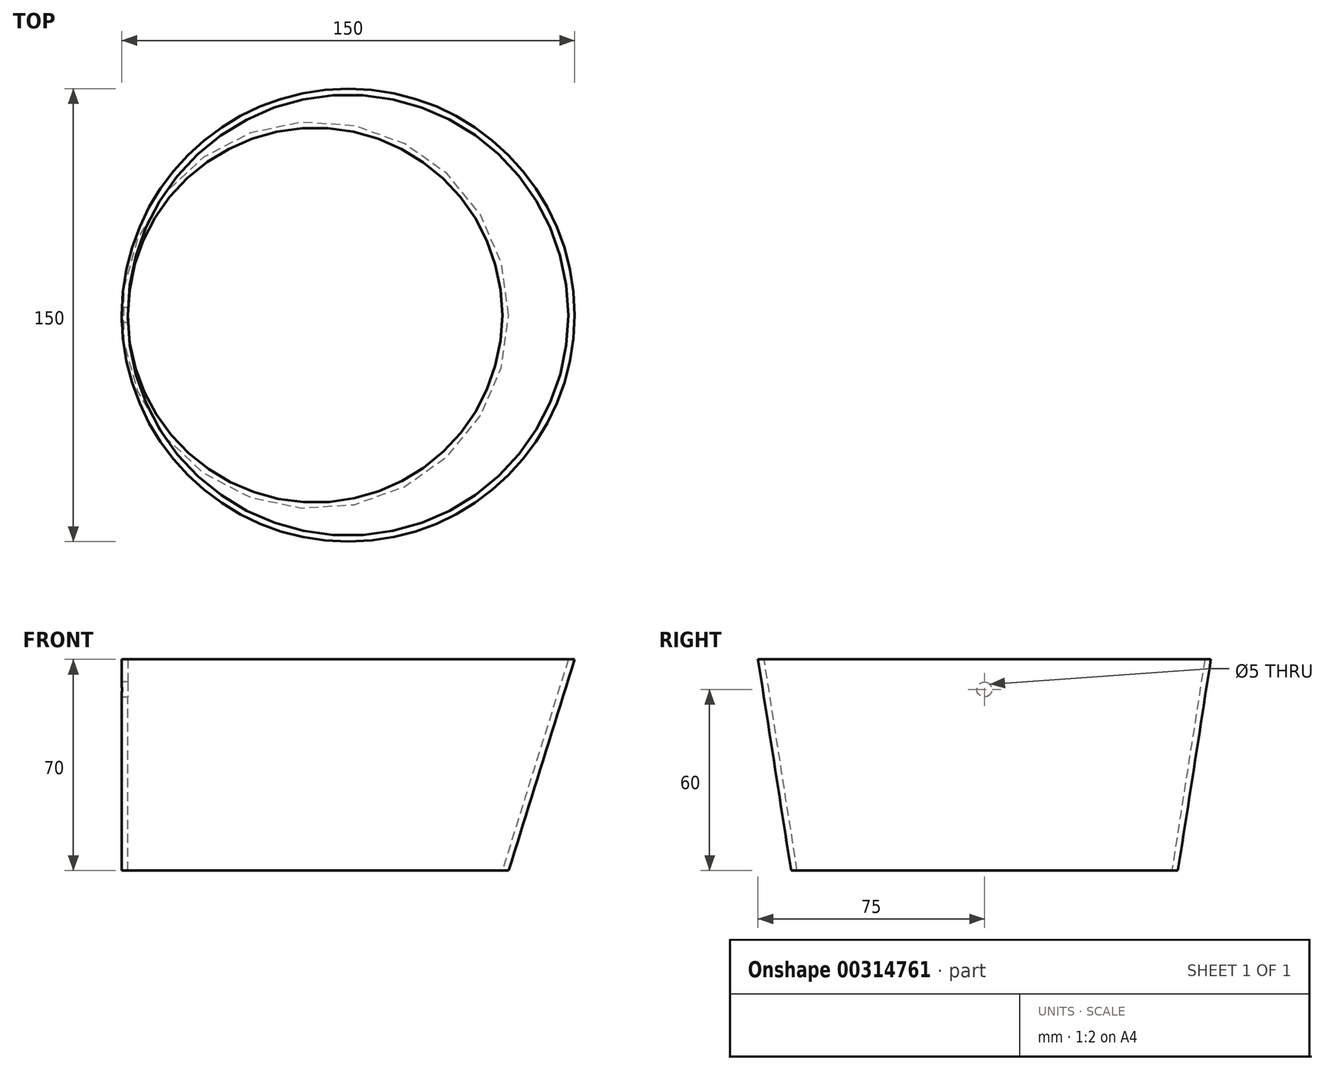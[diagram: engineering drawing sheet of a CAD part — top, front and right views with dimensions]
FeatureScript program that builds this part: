
annotation { "Feature Type Name" : "Feature", "Feature Type Description" : "" }
export const myFeature = defineFeature(function(context is Context, id is Id, definition is map)
    precondition{}
    {
        {
            var Q0;
            Q0=qCreatedBy(makeId("Top.planeOp"),FACE);
            var sketch = newSketch(context, id + "F0", { "sketchPlane" : qUnion([Q0])});
            skCircle(sketch, "E0", {"center": v(50, 0) * mm, "radius": 50 * mm});
            skSolve(sketch);
        }
        {
            var Q0;
            Q0=qCreatedBy(makeId("Top.planeOp"),FACE);
            cPlane(context, id + "F1", {"entities" : qUnion([Q0]), "cplaneType" : CPlaneType.OFFSET, "offset" : 160 * mm, "width" : 150 * mm, "height" : 150 * mm});
        }
        {
            var Q0;
            Q0=qCreatedBy(id+"F1.planeOp",FACE);
            var sketch = newSketch(context, id + "F2", { "sketchPlane" : qUnion([Q0])});
            skCircle(sketch, "E1", {"center": v(75, 0) * mm, "radius": 75 * mm});
            skSolve(sketch);
        }
        {
            var Q0;
            Q0=makeQuery(id+"F2.imprint","IMPRINT",FACE,{"disambiguationData":[TD([[makeQuery(id+"F2.imprint","IMPRINT",EDGE,{"derivedFrom":sQuery(id+"F2.wireOp",EDGE,"E1")}),1.0]])]});
            var Q1;
            Q1=makeQuery(id+"F0.imprint","IMPRINT",FACE,{"disambiguationData":[TD([[makeQuery(id+"F0.imprint","IMPRINT",EDGE,{"derivedFrom":sQuery(id+"F0.wireOp",EDGE,"E0")}),1.0]])]});
            loft(context, id + "F3", {"sheetProfilesArray" : [{ "sheetProfileEntities" : qUnion([Q0]) }, { "sheetProfileEntities" : qUnion([Q1]) }]});
        }
        {
            var Q0;
            Q0=makeQuery(id+"F3.opLoft","CAP_FACE",FACE,{"disambiguationData":[OSD([makeQuery(id+"F2.imprint","IMPRINT",FACE,{"disambiguationData":[TD([[makeQuery(id+"F2.imprint","IMPRINT",EDGE,{"derivedFrom":sQuery(id+"F2.wireOp",EDGE,"E1")}),1.0]])]})])],"isStart":true});
            shell(context, id + "F4", {"entities" : qUnion([Q0]), "thickness" : 2 * mm});
        }
        {
            var Q0;
            Q0=qCreatedBy(makeId("Right.planeOp"),FACE);
            var sketch = newSketch(context, id + "F5", { "sketchPlane" : qUnion([Q0])});
            skCircle(sketch, "E2", {"center": v(0, 150) * mm, "radius": 2.5 * mm});
            skCircle(sketch, "E3", {"center": v(0, 10) * mm, "radius": 2.5 * mm});
            skSolve(sketch);
        }
        {
            var Q0;
            Q0=qSketchRegion(id+"F5",true);
            extrude(context, id + "F6", {"entities" : qUnion([Q0]), "operationType" : NewBodyOperationType.REMOVE, "endBound" : BoundingType.UP_TO_NEXT, "depth" : 25 * mm});
        }
        {
            var Q0;
            Q0=makeQuery(id+"F3.opLoft","CAP_FACE",FACE,{"disambiguationData":[OSD([makeQuery(id+"F0.imprint","IMPRINT",FACE,{"disambiguationData":[TD([[makeQuery(id+"F0.imprint","IMPRINT",EDGE,{"derivedFrom":sQuery(id+"F0.wireOp",EDGE,"E0")}),1.0]])]})])],"isStart":true});
            var sketch = newSketch(context, id + "F7", { "sketchPlane" : qUnion([Q0])});
            skCircle(sketch, "E4", {"center": v(50, 0) * mm, "radius": 47.95 * mm});
            skSolve(sketch);
        }
        {
            var Q0;
            Q0=sQuery(id+"F7.wireOp",VERTEX,"E4.center");
            var Q1;
            Q1=makeQuery(id+"F3.opLoft","SWEPT_BODY",BODY,{"disambiguationData":[OSD([makeQuery(id+"F0.imprint","IMPRINT",FACE,{"disambiguationData":[TD([[makeQuery(id+"F0.imprint","IMPRINT",EDGE,{"derivedFrom":sQuery(id+"F0.wireOp",EDGE,"E0")}),1.0]])]}),makeQuery(id+"F2.imprint","IMPRINT",FACE,{"disambiguationData":[TD([[makeQuery(id+"F2.imprint","IMPRINT",EDGE,{"derivedFrom":sQuery(id+"F2.wireOp",EDGE,"E1")}),1.0]])]})])]});
            hole(context, id + "F8", {"style" : HoleStyle.C_BORE, "endStyle" : HoleEndStyle.THROUGH, "holeDiameter" : 15 * mm, "cBoreDiameter" : 97 * mm, "cBoreDepth" : 5 * mm, "isTappedThrough" : true, "tappedDepth" : 12 * mm, "tapClearance" : 3, "locations" : qUnion([Q0]), "scope" : qUnion([Q1])});
        }
        {
            var Q0;
            Q0=qCreatedBy(makeId("Front.planeOp"),FACE);
            var sketch = newSketch(context, id + "F9", { "sketchPlane" : qUnion([Q0])});
            skLineSegment(sketch, "E5.bottom", {"start": v(0, 0) * mm, "end": v(200, 0) * mm});
            skLineSegment(sketch, "E5.top", {"start": v(0, 90) * mm, "end": v(200, 90) * mm});
            skLineSegment(sketch, "E5.left", {"start": v(0, 0) * mm, "end": v(0, 90) * mm});
            skLineSegment(sketch, "E5.right", {"start": v(200, 0) * mm, "end": v(200, 90) * mm});
            skSolve(sketch);
        }
        {
            var Q0;
            Q0 = qSketchRegion(id + "F9", true);
            extrude(context, id + "F10", {"entities" : qUnion([Q0]), "operationType" : NewBodyOperationType.REMOVE, "endBound" : BoundingType.SYMMETRIC, "oppositeDirection" : true, "depth" : 200 * mm, "offsetDistance" : 25 * mm});
        }
    });
